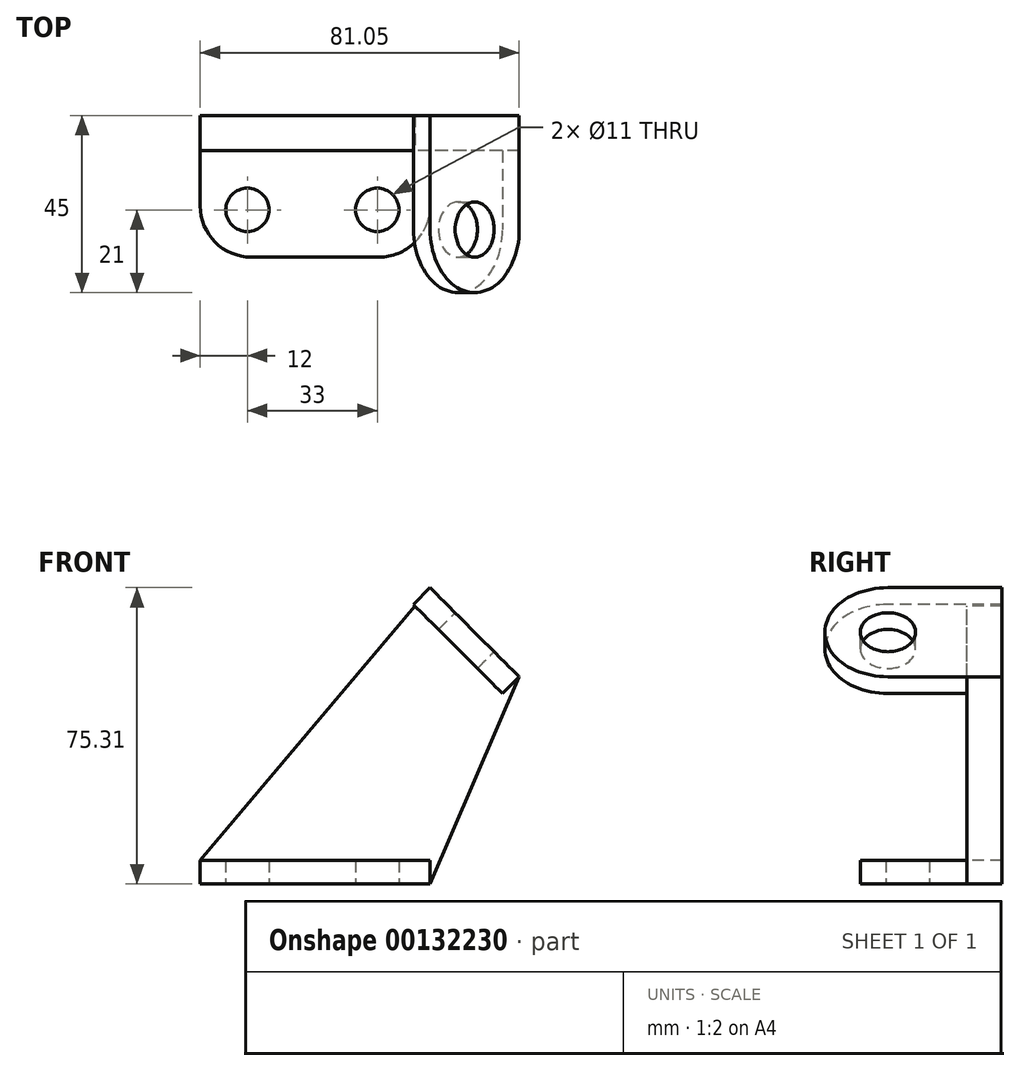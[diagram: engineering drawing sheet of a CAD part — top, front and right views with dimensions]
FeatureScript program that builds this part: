
annotation { "Feature Type Name" : "Feature", "Feature Type Description" : "" }
export const myFeature = defineFeature(function(context is Context, id is Id, definition is map)
    precondition{}
    {
        {
            var Q0;
            Q0=qCreatedBy(makeId("Front.planeOp"),FACE);
            var sketch = newSketch(context, id + "F0", { "sketchPlane" : qUnion([Q0])});
            skLineSegment(sketch, "E0", {"start": v(58.42, 75.31) * mm, "end": v(81.05, 52.69) * mm});
            skLineSegment(sketch, "E1", {"start": v(81.05, 52.69) * mm, "end": v(58.42, 0) * mm});
            skLineSegment(sketch, "E2", {"start": v(58.42, 0) * mm, "end": v(0, 0) * mm});
            skPoint(sketch, "E3", {"position": v(69.73, 64) * mm});
            skLineSegment(sketch, "E4", {"start": v(69.73, 64) * mm, "end": v(91.45, 64) * mm, "construction": true});
            skLineSegment(sketch, "E5", {"start": v(0, 0) * mm, "end": v(0, 6) * mm});
            skLineSegment(sketch, "E6", {"start": v(0, 6) * mm, "end": v(58.42, 75.31) * mm});
            skSolve(sketch);
        }
        {
            var Q0;
            Q0 = qSketchRegion(id + "F0", true);
            extrude(context, id + "F1", {"entities" : qUnion([Q0]), "oppositeDirection" : true, "depth" : 9 * mm});
        }
        {
            var Q0;
            Q0=qCreatedBy(makeId("Top.planeOp"),FACE);
            var sketch = newSketch(context, id + "F2", { "sketchPlane" : qUnion([Q0])});
            skLineSegment(sketch, "E7.bottom", {"start": v(0, 0) * mm, "end": v(58.42, 0) * mm});
            skLineSegment(sketch, "E7.top", {"start": v(13, -27) * mm, "end": v(45.42, -27) * mm});
            skLineSegment(sketch, "E7.left", {"start": v(0, 0) * mm, "end": v(0, -14) * mm});
            skLineSegment(sketch, "E7.right", {"start": v(58.42, 0) * mm, "end": v(58.42, -14) * mm});
            skCircle(sketch, "E8", {"center": v(12, -15) * mm, "radius": 5.5 * mm});
            skCircle(sketch, "E9", {"center": v(45, -15) * mm, "radius": 5.5 * mm});
            skPoint(sketch, "E10.visualSharp", {"position": v(58.42, -27) * mm});
            skArc(sketch, "E10.filletArc", {"start": v(45.42, -27) * mm, "mid": v(54.61, -23.2) * mm, "end": v(58.42, -14) * mm});
            skPoint(sketch, "E11.visualSharp", {"position": v(0, -27) * mm});
            skArc(sketch, "E11.filletArc", {"start": v(0, -14) * mm, "mid": v(3.8, -23.2) * mm, "end": v(13, -27) * mm});
            skSolve(sketch);
        }
        {
            var Q0;
            Q0 = qSketchRegion(id + "F2", true);
            extrude(context, id + "F3", {"entities" : qUnion([Q0]), "operationType" : NewBodyOperationType.ADD, "depth" : 6 * mm});
        }
        {
            var Q0;
            Q0=makeQuery(id+"F1.opExtrude","SWEPT_FACE",FACE,{"disambiguationData":[OSD([sQuery(id+"F0.wireOp",EDGE,"E0")])]});
            cPlane(context, id + "F4", {"entities" : qUnion([Q0]), "cplaneType" : CPlaneType.OFFSET, "offset" : 0 * mm, "width" : 150 * mm, "height" : 150 * mm});
        }
        {
            var Q0;
            Q0=qCreatedBy(id+"F4.planeOp",FACE);
            var sketch = newSketch(context, id + "F5", { "sketchPlane" : qUnion([Q0])});
            skLineSegment(sketch, "E12.bottom", {"start": v(9, 11.95) * mm, "end": v(-20, 11.95) * mm});
            skLineSegment(sketch, "E12.top", {"start": v(9, -20.05) * mm, "end": v(-20, -20.05) * mm});
            skLineSegment(sketch, "E12.left", {"start": v(9, 11.95) * mm, "end": v(9, -20.05) * mm});
            skLineSegment(sketch, "E12.right", {"start": v(-20, 11.95) * mm, "end": v(-20, -20.05) * mm, "construction": true});
            skArc(sketch, "E13", {"start": v(-20, 11.95) * mm, "mid": v(-36, -4.05) * mm, "end": v(-20, -20.05) * mm});
            skCircle(sketch, "E14", {"center": v(-20, -4.05) * mm, "radius": 7 * mm});
            skSolve(sketch);
        }
        {
            var Q0;
            Q0 = qSketchRegion(id + "F5", true);
            extrude(context, id + "F6", {"entities" : qUnion([Q0]), "operationType" : NewBodyOperationType.ADD, "oppositeDirection" : true, "depth" : 6 * mm});
        }
    });
